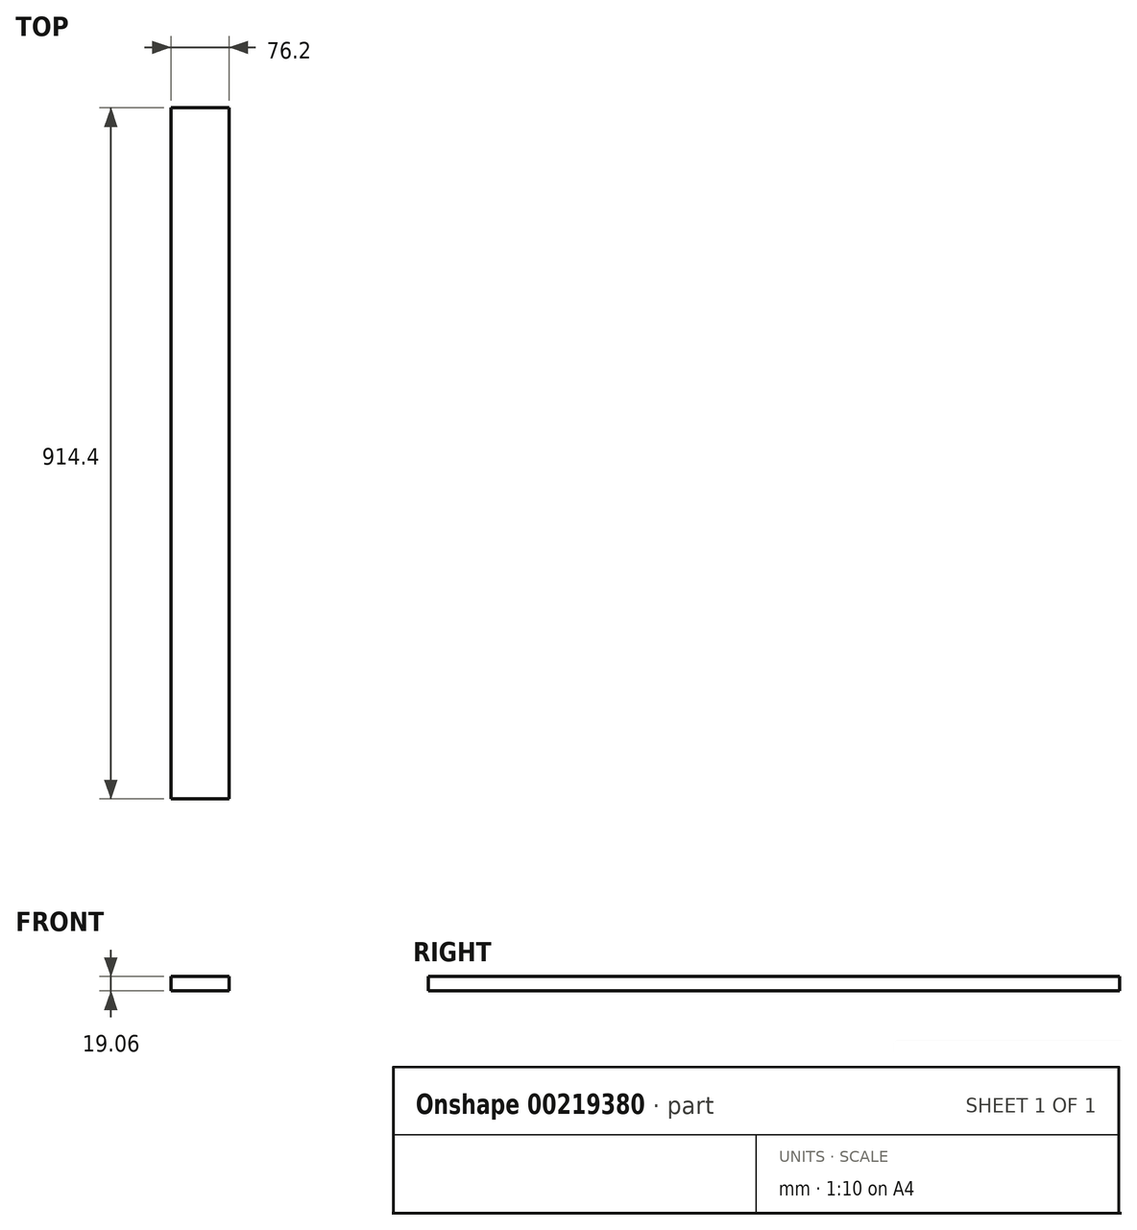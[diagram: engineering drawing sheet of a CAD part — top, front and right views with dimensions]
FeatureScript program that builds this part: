
annotation { "Feature Type Name" : "Feature", "Feature Type Description" : "" }
export const myFeature = defineFeature(function(context is Context, id is Id, definition is map)
    precondition{}
    {
        {
            var Q0;
            Q0=qCreatedBy(makeId("Front.planeOp"),FACE);
            var sketch = newSketch(context, id + "F0", { "sketchPlane" : qUnion([Q0])});
            skLineSegment(sketch, "E0.bottom", {"start": v(-38.1, 9.52) * mm, "end": v(38.1, 9.52) * mm});
            skLineSegment(sketch, "E0.top", {"start": v(-38.1, -9.52) * mm, "end": v(38.1, -9.52) * mm});
            skLineSegment(sketch, "E0.left", {"start": v(-38.1, 9.52) * mm, "end": v(-38.1, -9.52) * mm});
            skLineSegment(sketch, "E0.right", {"start": v(38.1, 9.52) * mm, "end": v(38.1, -9.52) * mm});
            skPoint(sketch, "E0.middle", {"position": v(0, 0) * mm});
            skSolve(sketch);
        }
        {
            var Q0;
            Q0 = qSketchRegion(id + "F0", true);
            extrude(context, id + "F1", {"entities" : qUnion([Q0]), "depth" : 914.4 * mm});
        }
    });
